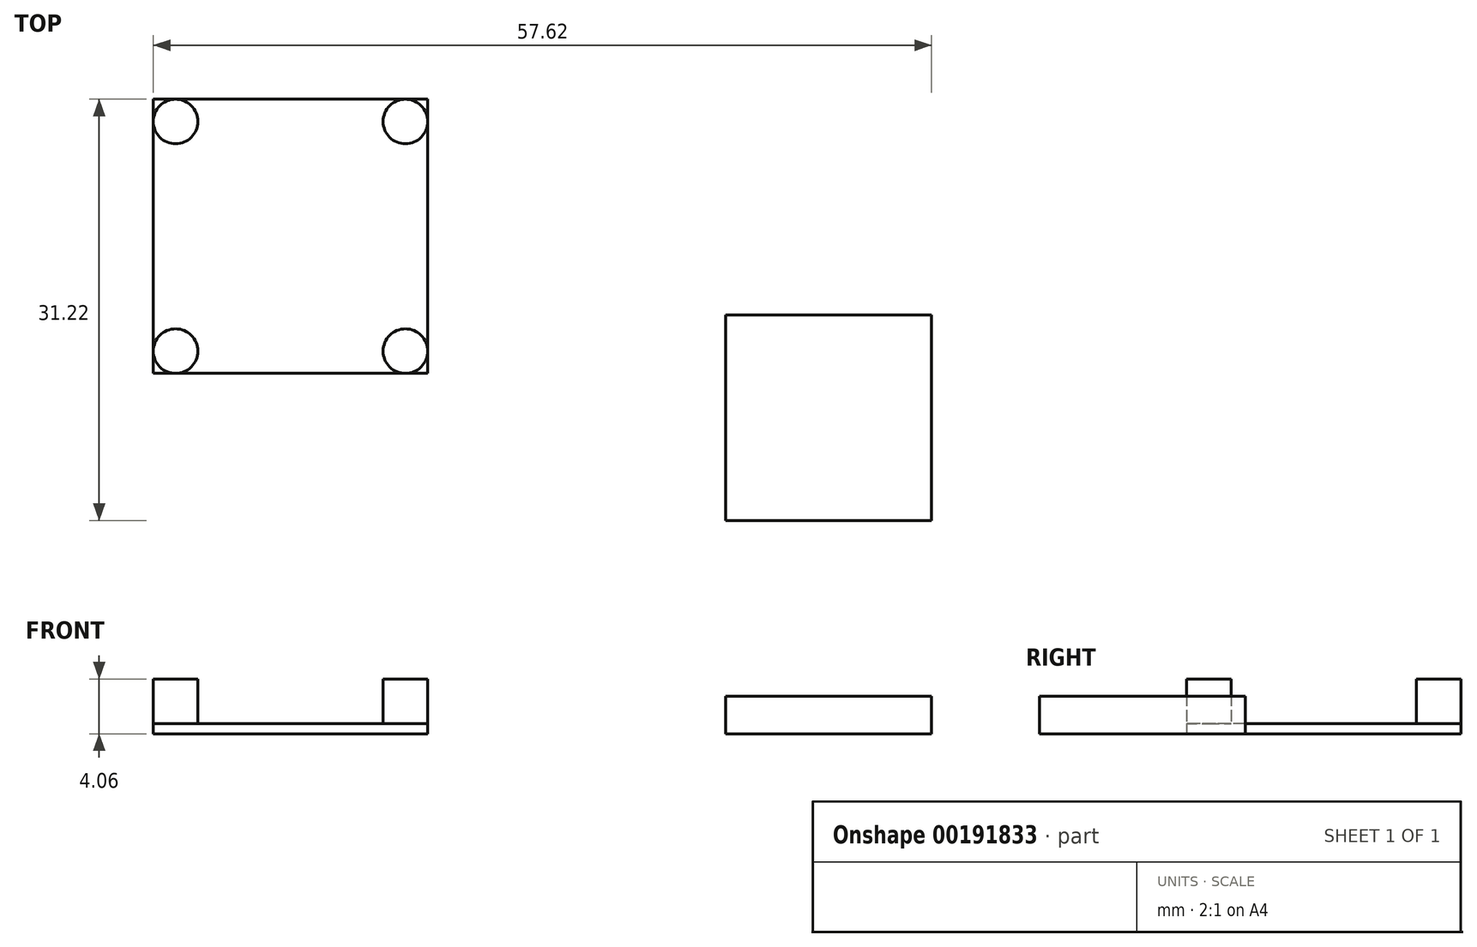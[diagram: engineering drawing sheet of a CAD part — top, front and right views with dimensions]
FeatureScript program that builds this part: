
annotation { "Feature Type Name" : "Feature", "Feature Type Description" : "" }
export const myFeature = defineFeature(function(context is Context, id is Id, definition is map)
    precondition{}
    {
        {
            var Q0;
            Q0=qCreatedBy(makeId("Top.planeOp"),FACE);
            var sketch = newSketch(context, id + "F0", { "sketchPlane" : qUnion([Q0])});
            skLineSegment(sketch, "E0.bottom", {"start": v(-55.28, 53.74) * mm, "end": v(-34.96, 53.74) * mm});
            skLineSegment(sketch, "E0.top", {"start": v(-55.28, 33.42) * mm, "end": v(-34.96, 33.42) * mm});
            skLineSegment(sketch, "E0.left", {"start": v(-55.28, 53.74) * mm, "end": v(-55.28, 33.42) * mm});
            skLineSegment(sketch, "E0.right", {"start": v(-34.96, 53.74) * mm, "end": v(-34.96, 33.42) * mm});
            skSolve(sketch);
        }
        {
            var Q0;
            Q0 = qSketchRegion(id + "F0", true);
            extrude(context, id + "F1", {"entities" : qUnion([Q0]), "depth" : 0.76 * mm});
        }
        {
            var Q0;
            Q0=makeQuery(id+"F1.opExtrude","CAP_FACE",FACE,{"disambiguationData":[OSD([sQuery(id+"F0.wireOp",EDGE,"E0.bottom"),sQuery(id+"F0.wireOp",EDGE,"E0.top"),sQuery(id+"F0.wireOp",EDGE,"E0.left"),sQuery(id+"F0.wireOp",EDGE,"E0.right")])],"isStart":false});
            var sketch = newSketch(context, id + "F2", { "sketchPlane" : qUnion([Q0])});
            skCircle(sketch, "E1", {"center": v(-36.61, 52.08) * mm, "radius": 1.65 * mm});
            skCircle(sketch, "E2", {"center": v(-53.63, 52.08) * mm, "radius": 1.65 * mm});
            skCircle(sketch, "E3", {"center": v(-53.63, 35.07) * mm, "radius": 1.65 * mm});
            skCircle(sketch, "E4", {"center": v(-36.61, 35.07) * mm, "radius": 1.65 * mm});
            skSolve(sketch);
        }
        {
            var Q0;
            Q0 = qSketchRegion(id + "F2", true);
            extrude(context, id + "F3", {"entities" : qUnion([Q0]), "depth" : 3.3 * mm});
        }
        {
            var Q0;
            Q0=qCreatedBy(makeId("Top.planeOp"),FACE);
            var sketch = newSketch(context, id + "F4", { "sketchPlane" : qUnion([Q0])});
            skLineSegment(sketch, "E5.bottom", {"start": v(2.34, 37.76) * mm, "end": v(-12.9, 37.76) * mm});
            skLineSegment(sketch, "E5.top", {"start": v(2.34, 22.52) * mm, "end": v(-12.9, 22.52) * mm});
            skLineSegment(sketch, "E5.left", {"start": v(2.34, 37.76) * mm, "end": v(2.34, 22.52) * mm});
            skLineSegment(sketch, "E5.right", {"start": v(-12.9, 37.76) * mm, "end": v(-12.9, 22.52) * mm});
            skSolve(sketch);
        }
        {
            var Q0;
            Q0 = qSketchRegion(id + "F4", true);
            extrude(context, id + "F5", {"entities" : qUnion([Q0]), "depth" : 2.8 * mm});
        }
    });
